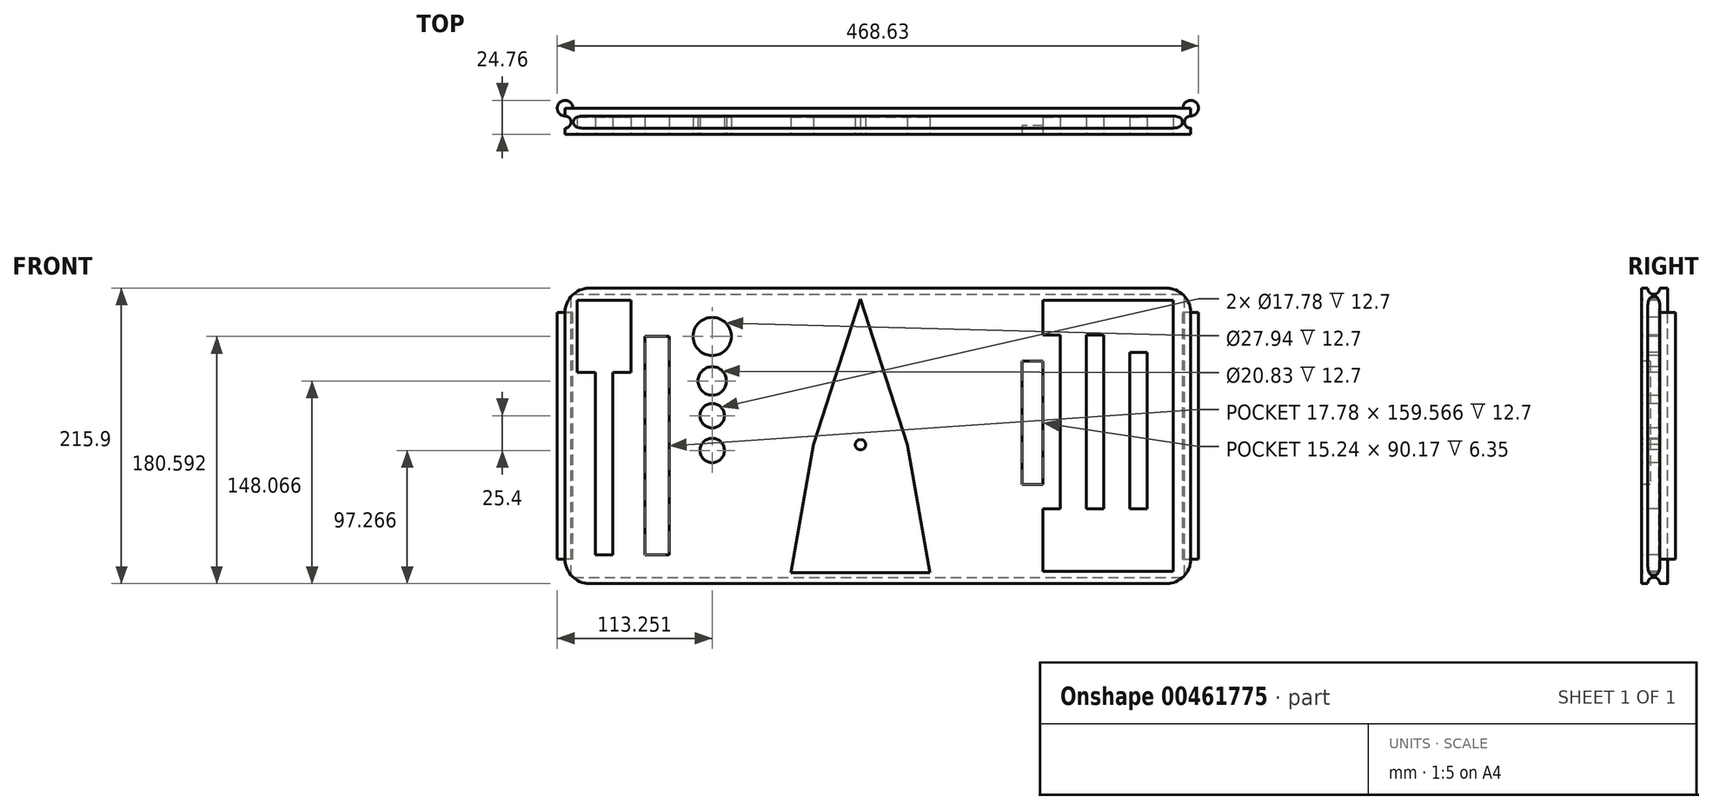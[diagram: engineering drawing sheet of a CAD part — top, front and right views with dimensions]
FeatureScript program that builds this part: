
annotation { "Feature Type Name" : "Feature", "Feature Type Description" : "" }
export const myFeature = defineFeature(function(context is Context, id is Id, definition is map)
    precondition{}
    {
        {
            var Q0;
            Q0=qCreatedBy(makeId("Front.planeOp"),FACE);
            var sketch = newSketch(context, id + "F0", { "sketchPlane" : qUnion([Q0])});
            skLineSegment(sketch, "E0.bottom", {"start": v(-137.99, 114.42) * mm, "end": v(319.21, 114.42) * mm});
            skLineSegment(sketch, "E0.top", {"start": v(-137.99, -101.48) * mm, "end": v(319.21, -101.48) * mm});
            skLineSegment(sketch, "E0.left", {"start": v(-137.99, 114.42) * mm, "end": v(-137.99, -101.48) * mm});
            skLineSegment(sketch, "E0.right", {"start": v(319.21, 114.42) * mm, "end": v(319.21, -101.48) * mm});
            skSolve(sketch);
        }
        {
            var Q0;
            Q0=makeQuery(id+"F0.imprint","IMPRINT",FACE,{"disambiguationData":[TD([[makeQuery(id+"F0.imprint","IMPRINT",EDGE,{"derivedFrom":sQuery(id+"F0.wireOp",EDGE,"E0.bottom")}),-1.0]])]});
            extrude(context, id + "F1", {"entities" : qUnion([Q0]), "depth" : 19.05 * mm});
        }
        {
            var Q0;
            Q0=makeQuery(id+"F1.opExtrude","CAP_FACE",FACE,{"disambiguationData":[OSD([sQuery(id+"F0.wireOp",EDGE,"E0.bottom"),sQuery(id+"F0.wireOp",EDGE,"E0.top"),sQuery(id+"F0.wireOp",EDGE,"E0.left"),sQuery(id+"F0.wireOp",EDGE,"E0.right")])],"isStart":false});
            var sketch = newSketch(context, id + "F2", { "sketchPlane" : qUnion([Q0])});
            skLineSegment(sketch, "E1.bottom", {"start": v(306.51, 105.53) * mm, "end": v(179.51, 105.53) * mm});
            skLineSegment(sketch, "E1.top", {"start": v(306.51, -92.6) * mm, "end": v(179.51, -92.6) * mm});
            skLineSegment(sketch, "E1.left", {"start": v(306.51, 105.53) * mm, "end": v(306.51, -92.6) * mm});
            skLineSegment(sketch, "E1.right", {"start": v(179.51, 105.53) * mm, "end": v(179.51, -92.6) * mm});
            skLineSegment(sketch, "E2.bottom", {"start": v(211.26, 80.13) * mm, "end": v(223.96, 80.13) * mm});
            skLineSegment(sketch, "E2.top", {"start": v(211.26, -46.87) * mm, "end": v(223.96, -46.87) * mm});
            skLineSegment(sketch, "E2.left", {"start": v(211.26, 80.13) * mm, "end": v(211.26, -46.87) * mm});
            skLineSegment(sketch, "E2.right", {"start": v(223.96, 80.13) * mm, "end": v(223.96, -46.87) * mm});
            skLineSegment(sketch, "E3", {"start": v(243, 80.13) * mm, "end": v(243, -46.87) * mm});
            skLineSegment(sketch, "E4", {"start": v(243, -46.87) * mm, "end": v(255.7, -46.87) * mm});
            skLineSegment(sketch, "E5", {"start": v(255.7, -46.87) * mm, "end": v(255.7, 80.13) * mm});
            skLineSegment(sketch, "E6", {"start": v(255.7, 80.13) * mm, "end": v(243, 80.13) * mm});
            skLineSegment(sketch, "E7", {"start": v(274.76, 80.13) * mm, "end": v(274.76, -46.87) * mm});
            skLineSegment(sketch, "E8", {"start": v(274.76, -46.87) * mm, "end": v(287.46, -46.87) * mm});
            skLineSegment(sketch, "E9", {"start": v(287.46, -46.87) * mm, "end": v(287.46, 80.13) * mm});
            skLineSegment(sketch, "E10", {"start": v(287.46, 80.13) * mm, "end": v(274.76, 80.13) * mm});
            skLineSegment(sketch, "E11", {"start": v(211.26, 80.13) * mm, "end": v(211.26, 105.53) * mm});
            skLineSegment(sketch, "E12", {"start": v(211.26, 105.53) * mm, "end": v(211.26, -46.87) * mm});
            skLineSegment(sketch, "E13", {"start": v(211.26, -92.6) * mm, "end": v(211.26, -46.87) * mm});
            skSolve(sketch);
        }
        {
            var Q0;
            Q0=makeQuery(id+"F1.opExtrude","CAP_FACE",FACE,{"disambiguationData":[OSD([sQuery(id+"F0.wireOp",EDGE,"E0.bottom"),sQuery(id+"F0.wireOp",EDGE,"E0.top"),sQuery(id+"F0.wireOp",EDGE,"E0.left"),sQuery(id+"F0.wireOp",EDGE,"E0.right")])],"isStart":false});
            var sketch = newSketch(context, id + "F3", { "sketchPlane" : qUnion([Q0])});
            skLineSegment(sketch, "E14", {"start": v(-137.99, 98.42) * mm, "end": v(-129.1, 98.42) * mm});
            skLineSegment(sketch, "E15", {"start": v(-112.55, 114.42) * mm, "end": v(-112.55, 105.53) * mm});
            skLineSegment(sketch, "E16", {"start": v(-129.1, 105.53) * mm, "end": v(-93.03, 105.53) * mm});
            skLineSegment(sketch, "E17.bottom", {"start": v(-129.1, 105.53) * mm, "end": v(-89.73, 105.53) * mm});
            skLineSegment(sketch, "E17.top", {"start": v(-129.1, 52.7) * mm, "end": v(-89.73, 52.7) * mm});
            skLineSegment(sketch, "E17.left", {"start": v(-129.1, 105.53) * mm, "end": v(-129.1, 52.7) * mm});
            skLineSegment(sketch, "E17.right", {"start": v(-89.73, 105.53) * mm, "end": v(-89.73, 52.7) * mm});
            skLineSegment(sketch, "E18", {"start": v(-129.1, 52.7) * mm, "end": v(-129.1, -80.65) * mm});
            skLineSegment(sketch, "E19", {"start": v(-109.41, 52.7) * mm, "end": v(-115.76, 52.7) * mm});
            skLineSegment(sketch, "E20", {"start": v(-115.76, 52.7) * mm, "end": v(-115.76, -80.65) * mm});
            skLineSegment(sketch, "E21", {"start": v(-115.76, -80.65) * mm, "end": v(-103.06, -80.65) * mm});
            skLineSegment(sketch, "E22", {"start": v(-103.06, -80.65) * mm, "end": v(-103.06, 52.7) * mm});
            skLineSegment(sketch, "E23", {"start": v(-79.57, 79.11) * mm, "end": v(-79.57, -80.45) * mm});
            skLineSegment(sketch, "E24", {"start": v(-79.57, -80.45) * mm, "end": v(-61.79, -80.45) * mm});
            skLineSegment(sketch, "E25", {"start": v(-61.79, -80.45) * mm, "end": v(-61.79, 79.11) * mm});
            skLineSegment(sketch, "E26", {"start": v(-61.79, 79.11) * mm, "end": v(-79.57, 79.11) * mm});
            skCircle(sketch, "E27", {"center": v(-30.45, 79.11) * mm, "radius": 13.97 * mm});
            skLineSegment(sketch, "E28", {"start": v(-30.45, 79.11) * mm, "end": v(-30.45, 46.59) * mm});
            skCircle(sketch, "E29", {"center": v(-30.45, 46.59) * mm, "radius": 10.41 * mm});
            skLineSegment(sketch, "E30", {"start": v(-30.45, 46.59) * mm, "end": v(-30.45, 21.19) * mm});
            skCircle(sketch, "E31", {"center": v(-30.45, 21.19) * mm, "radius": 8.9 * mm});
            skLineSegment(sketch, "E32", {"start": v(-30.45, 21.19) * mm, "end": v(-30.45, -4.21) * mm});
            skCircle(sketch, "E33", {"center": v(-30.45, -4.21) * mm, "radius": 8.9 * mm});
            skLineSegment(sketch, "E34", {"start": v(74.62, -93.56) * mm, "end": v(74.62, 106.47) * mm});
            skLineSegment(sketch, "E35", {"start": v(74.62, -93.56) * mm, "end": v(118.55, -93.56) * mm});
            skLineSegment(sketch, "E36", {"start": v(118.55, -93.56) * mm, "end": v(74.62, -93.56) * mm});
            skLineSegment(sketch, "E37", {"start": v(74.62, -93.56) * mm, "end": v(46.68, -93.56) * mm});
            skLineSegment(sketch, "E38", {"start": v(46.68, -93.56) * mm, "end": v(41.6, -93.56) * mm});
            skSolve(sketch);
        }
        {
            var Q0;
            {var subQ0=sQuery(id+"F2.wireOp",EDGE,"E1.left");Q0=makeQuery(id+"F2.imprint","IMPRINT",FACE,{"disambiguationData":[TD([[makeQuery(id+"F2.imprint","IMPRINT",EDGE,{"derivedFrom":subQ0}),-1.0]])]});}
            extrude(context, id + "F4", {"entities" : qUnion([Q0]), "operationType" : NewBodyOperationType.REMOVE, "oppositeDirection" : true, "depth" : 12.7 * mm});
        }
        {
            var Q0;
            {var subQ7=sQuery(id+"F3.wireOp",EDGE,"E17.right");Q0=makeQuery(id+"F3.imprint","IMPRINT",FACE,{"disambiguationData":[TD([[makeQuery(id+"F3.imprint","IMPRINT",EDGE,{"derivedFrom":subQ7}),-1.0]])]});}
            var Q1;
            {var subQ0=sQuery(id+"F3.wireOp",EDGE,"E19");Q1=makeQuery(id+"F3.imprint","IMPRINT",FACE,{"disambiguationData":[TD([[makeQuery(id+"F3.imprint","IMPRINT",EDGE,{"derivedFrom":subQ0}),1.0]])]});}
            extrude(context, id + "F5", {"entities" : qUnion([Q0, Q1]), "operationType" : NewBodyOperationType.REMOVE, "oppositeDirection" : true, "depth" : 12.7 * mm});
        }
        {
            var Q0;
            Q0 = qSketchRegion(id + "F3", true);
            extrude(context, id + "F6", {"entities" : qUnion([Q0]), "operationType" : NewBodyOperationType.REMOVE, "oppositeDirection" : true, "depth" : 12.7 * mm});
        }
        {
            var Q0;
            Q0 = qSketchRegion(id + "F3", true);
            extrude(context, id + "F7", {"entities" : qUnion([Q0]), "operationType" : NewBodyOperationType.REMOVE, "oppositeDirection" : true, "depth" : 12.7 * mm});
        }
        {
            var Q0;
            Q0=makeQuery(id+"F1.opExtrude","CAP_FACE",FACE,{"disambiguationData":[OSD([sQuery(id+"F0.wireOp",EDGE,"E0.bottom"),sQuery(id+"F0.wireOp",EDGE,"E0.top"),sQuery(id+"F0.wireOp",EDGE,"E0.left"),sQuery(id+"F0.wireOp",EDGE,"E0.right")])],"isStart":false});
            var sketch = newSketch(context, id + "F8", { "sketchPlane" : qUnion([Q0])});
            skLineSegment(sketch, "E39", {"start": v(77.91, -93.53) * mm, "end": v(77.91, 106.5) * mm});
            skLineSegment(sketch, "E40", {"start": v(77.91, -93.53) * mm, "end": v(116.01, -93.53) * mm});
            skLineSegment(sketch, "E41", {"start": v(77.91, -93.53) * mm, "end": v(27.11, -93.53) * mm});
            skLineSegment(sketch, "E42", {"start": v(116.01, -93.53) * mm, "end": v(128.71, -93.53) * mm});
            skLineSegment(sketch, "E43", {"start": v(27.11, -93.53) * mm, "end": v(43.6, 0) * mm});
            skLineSegment(sketch, "E44", {"start": v(43.6, 0) * mm, "end": v(77.91, 106.5) * mm});
            skLineSegment(sketch, "E45", {"start": v(128.71, -93.53) * mm, "end": v(112.22, 0) * mm});
            skLineSegment(sketch, "E46", {"start": v(112.22, 0) * mm, "end": v(77.91, 106.5) * mm});
            skCircle(sketch, "E47", {"center": v(77.91, 0) * mm, "radius": 3.81 * mm});
            skSolve(sketch);
        }
        {
            var Q0;
            Q0 = qSketchRegion(id + "F8", true);
            extrude(context, id + "F9", {"entities" : qUnion([Q0]), "operationType" : NewBodyOperationType.REMOVE, "oppositeDirection" : true, "depth" : 12.7 * mm});
        }
        {
            var Q0;
            Q0 = qSketchRegion(id + "F8", true);
            extrude(context, id + "F10", {"entities" : qUnion([Q0]), "operationType" : NewBodyOperationType.REMOVE, "oppositeDirection" : true, "depth" : 12.7 * mm});
        }
        {
            var Q0;
            {var subQ7=sQuery(id+"F0.wireOp",EDGE,"E0.left");var subQ11=sQuery(id+"F0.wireOp",EDGE,"E0.top");var subQ14=sQuery(id+"F0.wireOp",EDGE,"E0.right");var subQ17=sQuery(id+"F0.wireOp",EDGE,"E0.bottom");var subQ18=makeQuery(id+"F1.opExtrude","SWEPT_FACE",FACE,{"disambiguationData":[OSD([subQ17])]});Q0=makeQuery(id+"F9.boolean.opBoolean","SPLIT",FACE,{"disambiguationData":[TD([subQ18])],"derivedFrom":makeQuery(id+"F4.boolean.opBoolean","SPLIT",FACE,{"disambiguationData":[TD([subQ18])],"derivedFrom":makeQuery(id+"F1.opExtrude","CAP_FACE",FACE,{"disambiguationData":[OSD([subQ17,subQ11,subQ7,subQ14])],"isStart":false})})});}
            var sketch = newSketch(context, id + "F11", { "sketchPlane" : qUnion([Q0])});
            skLineSegment(sketch, "E48", {"start": v(211.26, 80.13) * mm, "end": v(211.26, 61.08) * mm});
            skLineSegment(sketch, "E49.bottom", {"start": v(211.26, 61.08) * mm, "end": v(196.02, 61.08) * mm});
            skLineSegment(sketch, "E49.top", {"start": v(211.26, -29.1) * mm, "end": v(196.02, -29.1) * mm});
            skLineSegment(sketch, "E49.left", {"start": v(211.26, 61.08) * mm, "end": v(211.26, -29.1) * mm});
            skLineSegment(sketch, "E49.right", {"start": v(196.02, 61.08) * mm, "end": v(196.02, -29.1) * mm});
            skSolve(sketch);
        }
        {
            var Q0;
            Q0=makeQuery(id+"F11.imprint","IMPRINT",FACE,{"disambiguationData":[TD([[makeQuery(id+"F11.imprint","IMPRINT",EDGE,{"derivedFrom":sQuery(id+"F11.wireOp",EDGE,"E49.bottom")}),1.0]])]});
            extrude(context, id + "F12", {"entities" : qUnion([Q0]), "operationType" : NewBodyOperationType.REMOVE, "oppositeDirection" : true, "depth" : 6.35 * mm});
        }
        {
            var Q0;
            Q0=makeQuery(id+"F1.opExtrude","SWEPT_EDGE",EDGE,{"disambiguationData":[OSD([sQuery(id+"F0.wireOp",EDGE,"E0.bottom"),sQuery(id+"F0.wireOp",EDGE,"E0.left")])]});
            var Q1;
            Q1=makeQuery(id+"F1.opExtrude","SWEPT_EDGE",EDGE,{"disambiguationData":[OSD([sQuery(id+"F0.wireOp",EDGE,"E0.bottom"),sQuery(id+"F0.wireOp",EDGE,"E0.right")])]});
            var Q2;
            Q2=makeQuery(id+"F1.opExtrude","SWEPT_EDGE",EDGE,{"disambiguationData":[OSD([sQuery(id+"F0.wireOp",EDGE,"E0.top"),sQuery(id+"F0.wireOp",EDGE,"E0.right")])]});
            var Q3;
            Q3=makeQuery(id+"F1.opExtrude","SWEPT_EDGE",EDGE,{"disambiguationData":[OSD([sQuery(id+"F0.wireOp",EDGE,"E0.top"),sQuery(id+"F0.wireOp",EDGE,"E0.left")])]});
            fillet(context, id + "F13", {"entities" : qUnion([Q0, Q1, Q2, Q3]), "radius" : 17.78 * mm, "tangentPropagation" : true, "allowEdgeOverflow" : false});
        }
        {
            var Q0;
            Q0=makeQuery(id+"F1.opExtrude","SWEPT_FACE",FACE,{"disambiguationData":[OSD([sQuery(id+"F0.wireOp",EDGE,"E0.right")])]});
            var sketch = newSketch(context, id + "F14", { "sketchPlane" : qUnion([Q0])});
            skLineSegment(sketch, "E50", {"start": v(-19.05, 96.64) * mm, "end": v(-19.05, 114.42) * mm});
            skLineSegment(sketch, "E51", {"start": v(-19.05, 114.42) * mm, "end": v(-10.16, 114.42) * mm});
            skCircle(sketch, "E52", {"center": v(-10.16, 114.42) * mm, "radius": 4.45 * mm});
            skSolve(sketch);
        }
        {
            var Q0;
            Q0=makeQuery(id+"F14.imprint","IMPRINT",FACE,{"disambiguationData":[TD([[makeQuery(id+"F14.imprint","IMPRINT",EDGE,{"derivedFrom":sQuery(id+"F14.wireOp",EDGE,"E52")}),1.0]])]});
            extrude(context, id + "F15", {"entities" : qUnion([Q0]), "operationType" : NewBodyOperationType.REMOVE, "oppositeDirection" : true, "depth" : 469.9 * mm});
        }
        {
            var Q0;
            {var subQ0=sQuery(id+"F0.wireOp",EDGE,"E0.right");var subQ1=sQuery(id+"F0.wireOp",EDGE,"E0.left");var subQ2=sQuery(id+"F0.wireOp",EDGE,"E0.bottom");Q0=makeQuery(id+"F15.boolean.opBoolean","SPLIT",FACE,{"disambiguationData":[TD([makeQuery(id+"F1.opExtrude","CAP_FACE",FACE,{"disambiguationData":[OSD([subQ2,sQuery(id+"F0.wireOp",EDGE,"E0.top"),subQ1,subQ0])],"isStart":true})])],"derivedFrom":makeQuery(id+"F1.opExtrude","SWEPT_FACE",FACE,{"disambiguationData":[OSD([subQ2])]})});}
            var sketch = newSketch(context, id + "F16", { "sketchPlane" : qUnion([Q0])});
            skLineSegment(sketch, "E53", {"start": v(301.43, 0) * mm, "end": v(319.21, 0) * mm});
            skLineSegment(sketch, "E54", {"start": v(319.21, 0) * mm, "end": v(319.21, -10.16) * mm});
            skCircle(sketch, "E55", {"center": v(319.21, -10.16) * mm, "radius": 4.45 * mm});
            skSolve(sketch);
        }
        {
            var Q0;
            Q0 = qSketchRegion(id + "F16", true);
            extrude(context, id + "F17", {"entities" : qUnion([Q0]), "operationType" : NewBodyOperationType.REMOVE, "oppositeDirection" : true, "depth" : 215.9 * mm});
        }
        {
            var Q0;
            {var subQ0=sQuery(id+"F0.wireOp",EDGE,"E0.right");var subQ1=sQuery(id+"F0.wireOp",EDGE,"E0.left");var subQ2=sQuery(id+"F0.wireOp",EDGE,"E0.bottom");Q0=makeQuery(id+"F15.boolean.opBoolean","SPLIT",FACE,{"disambiguationData":[TD([makeQuery(id+"F1.opExtrude","CAP_FACE",FACE,{"disambiguationData":[OSD([subQ2,sQuery(id+"F0.wireOp",EDGE,"E0.top"),subQ1,subQ0])],"isStart":false})])],"derivedFrom":makeQuery(id+"F1.opExtrude","SWEPT_FACE",FACE,{"disambiguationData":[OSD([subQ2])]})});}
            var sketch = newSketch(context, id + "F18", { "sketchPlane" : qUnion([Q0])});
            skLineSegment(sketch, "E56", {"start": v(-120.2, -19.05) * mm, "end": v(-137.99, -19.05) * mm});
            skLineSegment(sketch, "E57", {"start": v(-137.99, -19.05) * mm, "end": v(-137.99, -10.16) * mm});
            skCircle(sketch, "E58", {"center": v(-137.99, -10.16) * mm, "radius": 4.45 * mm});
            skSolve(sketch);
        }
        {
            var Q0;
            Q0 = qSketchRegion(id + "F18", true);
            extrude(context, id + "F19", {"entities" : qUnion([Q0]), "operationType" : NewBodyOperationType.REMOVE, "oppositeDirection" : true, "depth" : 215.9 * mm});
        }
        {
            var Q0;
            {var subQ0=sQuery(id+"F0.wireOp",EDGE,"E0.right");var subQ1=sQuery(id+"F0.wireOp",EDGE,"E0.top");var subQ2=sQuery(id+"F0.wireOp",EDGE,"E0.bottom");Q0=makeQuery(id+"F17.boolean.opBoolean","SPLIT",FACE,{"disambiguationData":[TD([makeQuery(id+"F1.opExtrude","CAP_FACE",FACE,{"disambiguationData":[OSD([subQ2,subQ1,sQuery(id+"F0.wireOp",EDGE,"E0.left"),subQ0])],"isStart":false})])],"derivedFrom":makeQuery(id+"F1.opExtrude","SWEPT_FACE",FACE,{"disambiguationData":[OSD([subQ0])]})});}
            var sketch = newSketch(context, id + "F20", { "sketchPlane" : qUnion([Q0])});
            skLineSegment(sketch, "E59", {"start": v(-19.05, -83.7) * mm, "end": v(-19.05, -101.48) * mm});
            skLineSegment(sketch, "E60", {"start": v(-19.05, -101.48) * mm, "end": v(-10.16, -101.48) * mm});
            skCircle(sketch, "E61", {"center": v(-10.16, -101.48) * mm, "radius": 4.45 * mm});
            skSolve(sketch);
        }
        {
            var Q0;
            Q0 = qSketchRegion(id + "F20", true);
            extrude(context, id + "F21", {"entities" : qUnion([Q0]), "operationType" : NewBodyOperationType.REMOVE, "oppositeDirection" : true, "depth" : 457.2 * mm});
        }
        {
            var Q0;
            Q0=makeQuery(id+"F4.boolean.opBoolean","SPLIT",FACE,{"disambiguationData":[TD([makeQuery(id+"F4.opExtrude","SWEPT_FACE",FACE,{"disambiguationData":[OSD([sQuery(id+"F2.wireOp",EDGE,"E7")])]})])],"derivedFrom":makeQuery(id+"F1.opExtrude","CAP_FACE",FACE,{"disambiguationData":[OSD([sQuery(id+"F0.wireOp",EDGE,"E0.bottom"),sQuery(id+"F0.wireOp",EDGE,"E0.top"),sQuery(id+"F0.wireOp",EDGE,"E0.left"),sQuery(id+"F0.wireOp",EDGE,"E0.right")])],"isStart":false})});
            var sketch = newSketch(context, id + "F22", { "sketchPlane" : qUnion([Q0])});
            skLineSegment(sketch, "E62.bottom", {"start": v(274.76, 80.13) * mm, "end": v(287.46, 80.13) * mm});
            skLineSegment(sketch, "E62.top", {"start": v(274.76, 67.43) * mm, "end": v(287.46, 67.43) * mm});
            skLineSegment(sketch, "E62.left", {"start": v(274.76, 80.13) * mm, "end": v(274.76, 67.43) * mm});
            skLineSegment(sketch, "E62.right", {"start": v(287.46, 80.13) * mm, "end": v(287.46, 67.43) * mm});
            skSolve(sketch);
        }
        {
            var Q0;
            Q0 = qSketchRegion(id + "F22", true);
            extrude(context, id + "F23", {"entities" : qUnion([Q0]), "operationType" : NewBodyOperationType.REMOVE, "oppositeDirection" : true, "depth" : 12.7 * mm});
        }
        {
            var Q0;
            {var subQ0=sQuery(id+"F0.wireOp",EDGE,"E0.right");var subQ1=sQuery(id+"F0.wireOp",EDGE,"E0.top");var subQ2=sQuery(id+"F0.wireOp",EDGE,"E0.bottom");Q0=makeQuery(id+"F17.boolean.opBoolean","SPLIT",FACE,{"disambiguationData":[TD([makeQuery(id+"F1.opExtrude","CAP_FACE",FACE,{"disambiguationData":[OSD([subQ2,subQ1,sQuery(id+"F0.wireOp",EDGE,"E0.left"),subQ0])],"isStart":true})])],"derivedFrom":makeQuery(id+"F1.opExtrude","SWEPT_FACE",FACE,{"disambiguationData":[OSD([subQ0])]})});}
            var Q1;
            Q1=makeQuery(id+"F1.opExtrude","CAP_EDGE",EDGE,{"disambiguationData":[OSD([sQuery(id+"F0.wireOp",EDGE,"E0.right")])],"isStart":true});
            revolve(context, id + "F24", {"operationType" : NewBodyOperationType.ADD, "entities" : qUnion([Q0]), "axis" : qUnion([Q1]), "revolveType" : RevolveType.FULL});
        }
        {
            var Q0;
            {var subQ0=sQuery(id+"F0.wireOp",EDGE,"E0.left");var subQ1=sQuery(id+"F0.wireOp",EDGE,"E0.top");var subQ2=sQuery(id+"F0.wireOp",EDGE,"E0.bottom");Q0=makeQuery(id+"F19.boolean.opBoolean","SPLIT",FACE,{"disambiguationData":[TD([makeQuery(id+"F1.opExtrude","CAP_FACE",FACE,{"disambiguationData":[OSD([subQ2,subQ1,subQ0,sQuery(id+"F0.wireOp",EDGE,"E0.right")])],"isStart":true})])],"derivedFrom":makeQuery(id+"F1.opExtrude","SWEPT_FACE",FACE,{"disambiguationData":[OSD([subQ0])]})});}
            var Q1;
            Q1=makeQuery(id+"F1.opExtrude","CAP_EDGE",EDGE,{"disambiguationData":[OSD([sQuery(id+"F0.wireOp",EDGE,"E0.left")])],"isStart":true});
            revolve(context, id + "F25", {"operationType" : NewBodyOperationType.ADD, "entities" : qUnion([Q0]), "axis" : qUnion([Q1]), "revolveType" : RevolveType.FULL});
        }
    });
